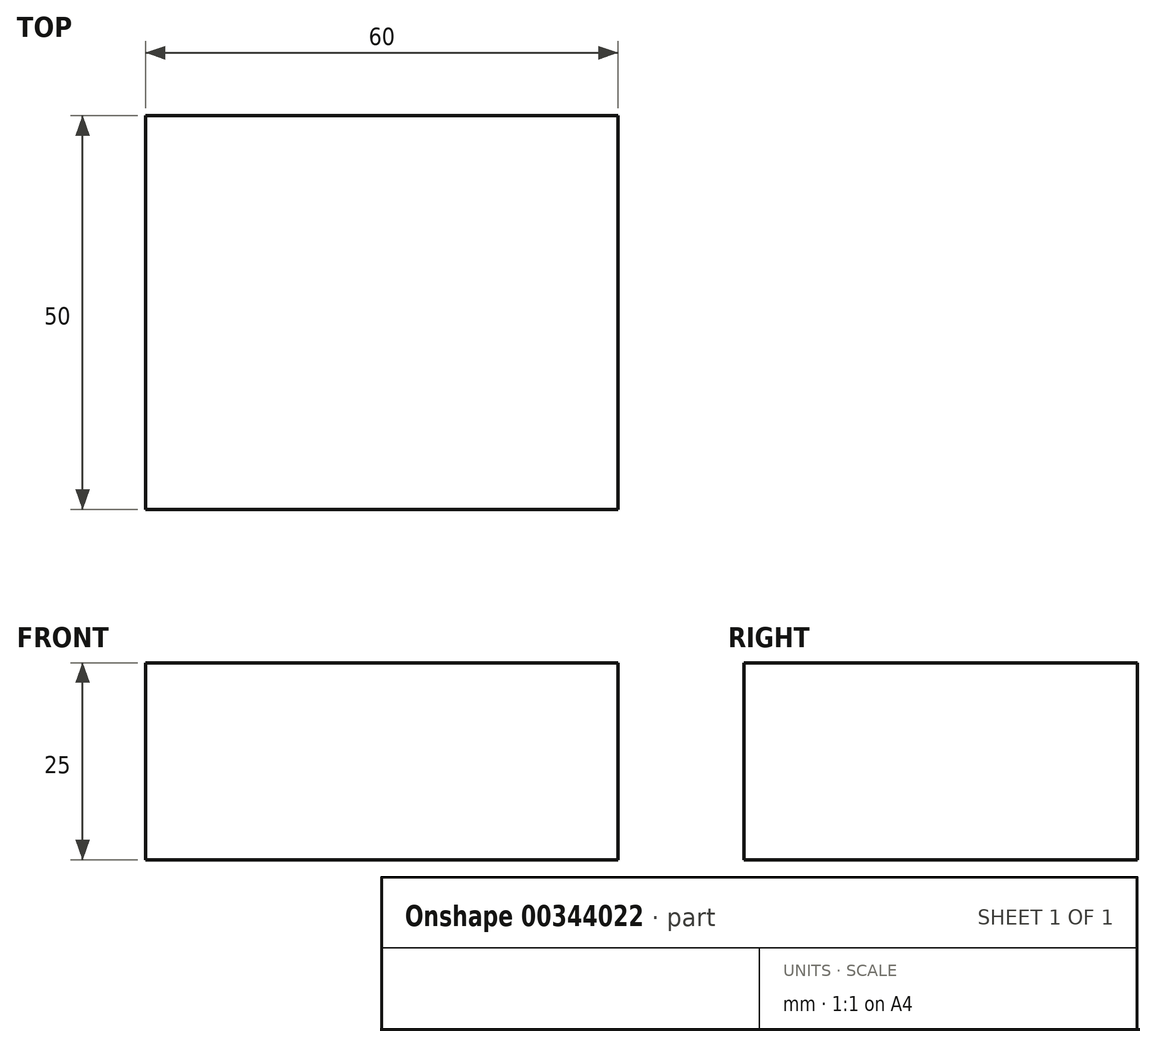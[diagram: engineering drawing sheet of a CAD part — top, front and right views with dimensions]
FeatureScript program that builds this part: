
annotation { "Feature Type Name" : "Feature", "Feature Type Description" : "" }
export const myFeature = defineFeature(function(context is Context, id is Id, definition is map)
    precondition{}
    {
        {
            var Q0;
            Q0=qCreatedBy(makeId("Top.planeOp"),FACE);
            var sketch = newSketch(context, id + "F0", { "sketchPlane" : qUnion([Q0])});
            skLineSegment(sketch, "E0.bottom", {"start": v(-106.41, 29.45) * mm, "end": v(-46.41, 29.45) * mm});
            skLineSegment(sketch, "E0.top", {"start": v(-106.41, -20.55) * mm, "end": v(-46.41, -20.55) * mm});
            skLineSegment(sketch, "E0.left", {"start": v(-106.41, 29.45) * mm, "end": v(-106.41, -20.55) * mm});
            skLineSegment(sketch, "E0.right", {"start": v(-46.41, 29.45) * mm, "end": v(-46.41, -20.55) * mm});
            skSolve(sketch);
        }
        {
            var Q0;
            Q0 = qSketchRegion(id + "F0", true);
            extrude(context, id + "F1", {"entities" : qUnion([Q0]), "depth" : 25 * mm});
        }
    });
